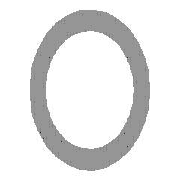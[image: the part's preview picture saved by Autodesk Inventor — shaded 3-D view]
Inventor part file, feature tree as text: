
AUTODESK INVENTOR PART (.ipt)
format: ipt  version: 2021 (Build 250183000, 183)  size: 159,744 bytes
history: native  units: mm (DEFAULTED — no unit token found)
features: other x10, sketch x4, extrude x2, plane x1
ambient origin geometry x8: Origin, YZ Plane, XZ Plane, XY Plane, X Axis, Y Axis, Z Axis, Center Point
bodies: Solid1 (feature_tree)
feature tree (17):
  parser-record x1  (decoder bookkeeping rows leaked as tree rows — omitted from the tree; the rows remain in map.json)
  other  "Driven Length"
  other  "Plano inicial"
  other  "Plano final"
  extrude  "Cuerpo"  Depth=4.8514mm
  extrude  "Extrusión2"  TaperAngle=0.0deg  [1 undecoded]
  sketch  "Boceto"  dims[d6=90.0deg d7=550.0mm d84=5.0mm d85=40.0mm d86=0.0mm d199=5.0mm d200=0.0mm d201=5.0mm d202=0.0mm]
  sketch  "Sketch3"  dims[d0=42.164mm d1=4.8514mm]
  plane  "Work Plane3"
  sketch  "Sketch4"  dims[d2=528.33989mm d3=0.0mm d4=-0.0mm]
  sketch  "Boceto5"  dims[d5=550.0mm]
  other  "Sup143"
  other  "Sup144"
  other  "Sólido49"
  other  "Sup142"
  other  "Superficie de contorno95"
  other  "Superficie de contorno96"
note: 1 required parameter value undecoded (feature->parameter linkage not recoverable at this tier; creation-order binding heuristic only, values carry confidence <= 0.55)
